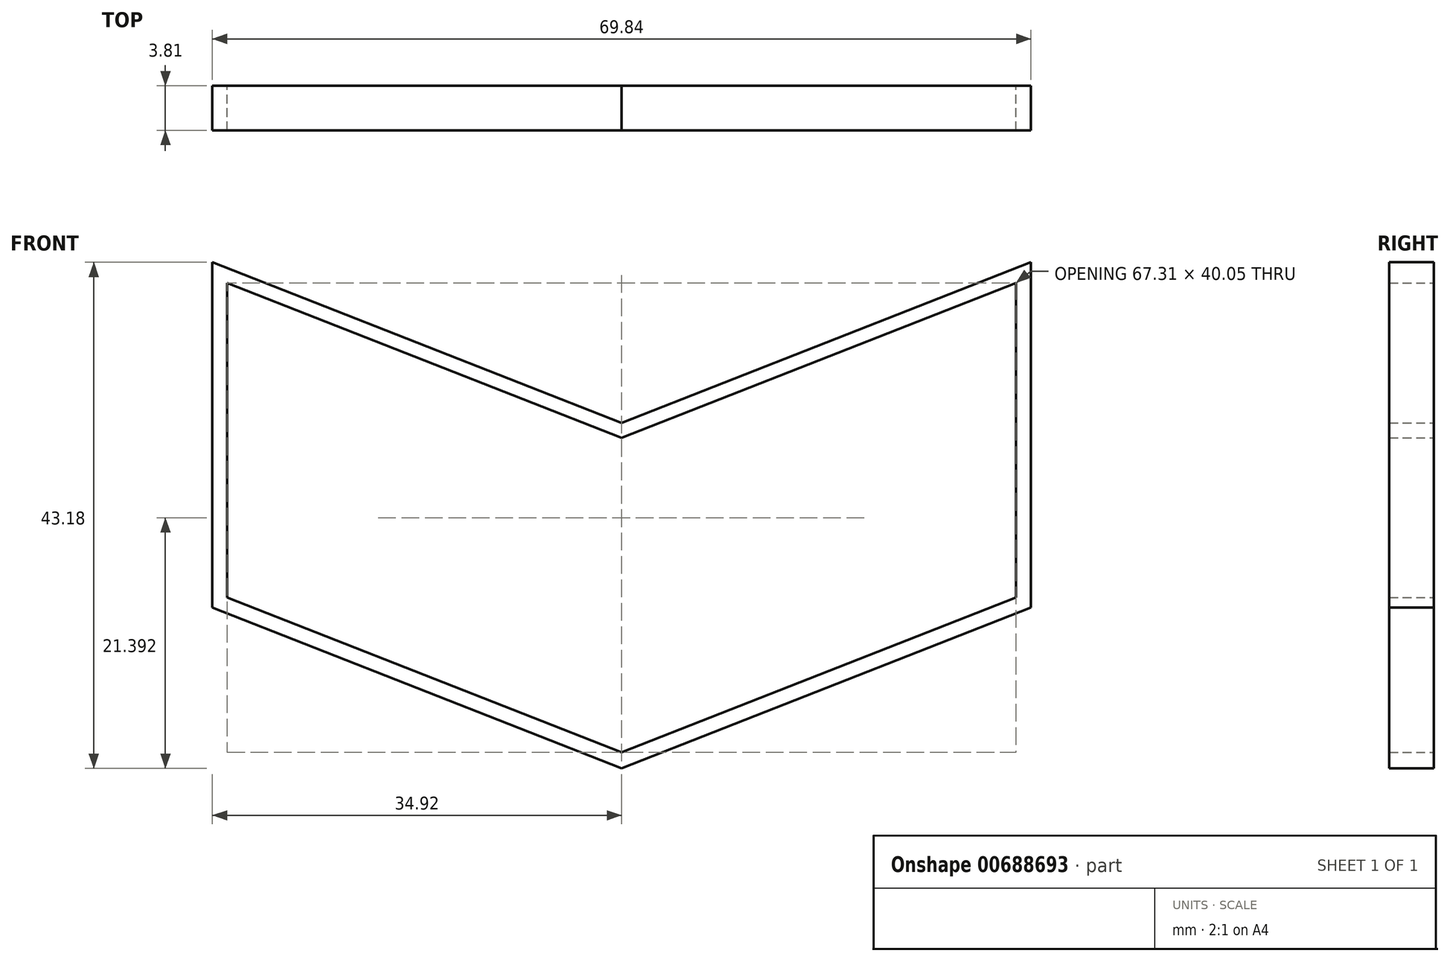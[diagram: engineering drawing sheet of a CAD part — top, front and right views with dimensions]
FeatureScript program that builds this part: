
annotation { "Feature Type Name" : "Feature", "Feature Type Description" : "" }
export const myFeature = defineFeature(function(context is Context, id is Id, definition is map)
    precondition{}
    {
        {
            var Q0;
            Q0=qCreatedBy(makeId("Front.planeOp"),FACE);
            var sketch = newSketch(context, id + "F0", { "sketchPlane" : qUnion([Q0])});
            skLineSegment(sketch, "E0", {"start": v(0, 4.93) * mm, "end": v(0, -24.53) * mm});
            skLineSegment(sketch, "E1", {"start": v(0, -24.53) * mm, "end": v(-34.92, -10.8) * mm});
            skLineSegment(sketch, "E2", {"start": v(0, 4.93) * mm, "end": v(-34.93, 18.65) * mm});
            skLineSegment(sketch, "E3", {"start": v(-34.93, 18.65) * mm, "end": v(-34.92, -10.8) * mm});
            skLineSegment(sketch, "E4", {"start": v(0, -2.69) * mm, "end": v(-27.3, 7.55) * mm});
            skLineSegment(sketch, "E5", {"start": v(-27.3, 7.55) * mm, "end": v(-27.3, -6.67) * mm});
            skLineSegment(sketch, "E6", {"start": v(-27.3, -6.67) * mm, "end": v(0, -16.9) * mm});
            skLineSegment(sketch, "E7.MirrorCS", {"start": v(0, 4.93) * mm, "end": v(34.93, 18.65) * mm});
            skLineSegment(sketch, "E8.MirrorCS", {"start": v(34.93, 18.65) * mm, "end": v(34.93, -10.8) * mm});
            skLineSegment(sketch, "E9.MirrorCS", {"start": v(0, -24.53) * mm, "end": v(34.92, -10.8) * mm});
            skLineSegment(sketch, "E10.MirrorCS", {"start": v(27.3, -6.67) * mm, "end": v(0, -16.9) * mm});
            skLineSegment(sketch, "E11.MirrorCS", {"start": v(27.3, 7.55) * mm, "end": v(27.3, -6.67) * mm});
            skLineSegment(sketch, "E12.MirrorCS", {"start": v(0, -2.69) * mm, "end": v(27.3, 7.55) * mm});
            skLineSegment(sketch, "E13", {"start": v(0, 4.93) * mm, "end": v(0, 0) * mm});
            skLineSegment(sketch, "E14", {"start": v(0, -24.53) * mm, "end": v(0, -16.9) * mm});
            skLineSegment(sketch, "E15", {"start": v(-33.66, 16.89) * mm, "end": v(-33.65, -9.94) * mm});
            skLineSegment(sketch, "E16", {"start": v(-33.66, -9.94) * mm, "end": v(0, -23.16) * mm});
            skLineSegment(sketch, "E17", {"start": v(0, -23.16) * mm, "end": v(33.65, -9.94) * mm});
            skLineSegment(sketch, "E18", {"start": v(33.65, -9.94) * mm, "end": v(33.65, 16.89) * mm});
            skLineSegment(sketch, "E19", {"start": v(33.66, 16.89) * mm, "end": v(0, 3.66) * mm});
            skLineSegment(sketch, "E20", {"start": v(0, 3.66) * mm, "end": v(-33.66, 16.89) * mm});
            skLineSegment(sketch, "E21", {"start": v(0, -1.2) * mm, "end": v(28.58, 9.51) * mm});
            skLineSegment(sketch, "E22", {"start": v(28.57, 9.51) * mm, "end": v(28.57, -7.63) * mm});
            skLineSegment(sketch, "E23", {"start": v(28.57, -7.63) * mm, "end": v(0, -18.22) * mm});
            skLineSegment(sketch, "E24", {"start": v(0, -18.22) * mm, "end": v(-28.58, -7.5) * mm});
            skLineSegment(sketch, "E25", {"start": v(-28.57, -7.5) * mm, "end": v(-28.57, 9.55) * mm});
            skLineSegment(sketch, "E26", {"start": v(0, -1.2) * mm, "end": v(-28.58, 9.51) * mm});
            skSolve(sketch);
        }
        {
            var Q0;
            Q0=qSketchRegion(id+"F0",true);
            extrude(context, id + "F1", {"entities" : qUnion([Q0]), "depth" : 3.8 * mm, "offsetDistance" : 25.4 * mm});
        }
    });
